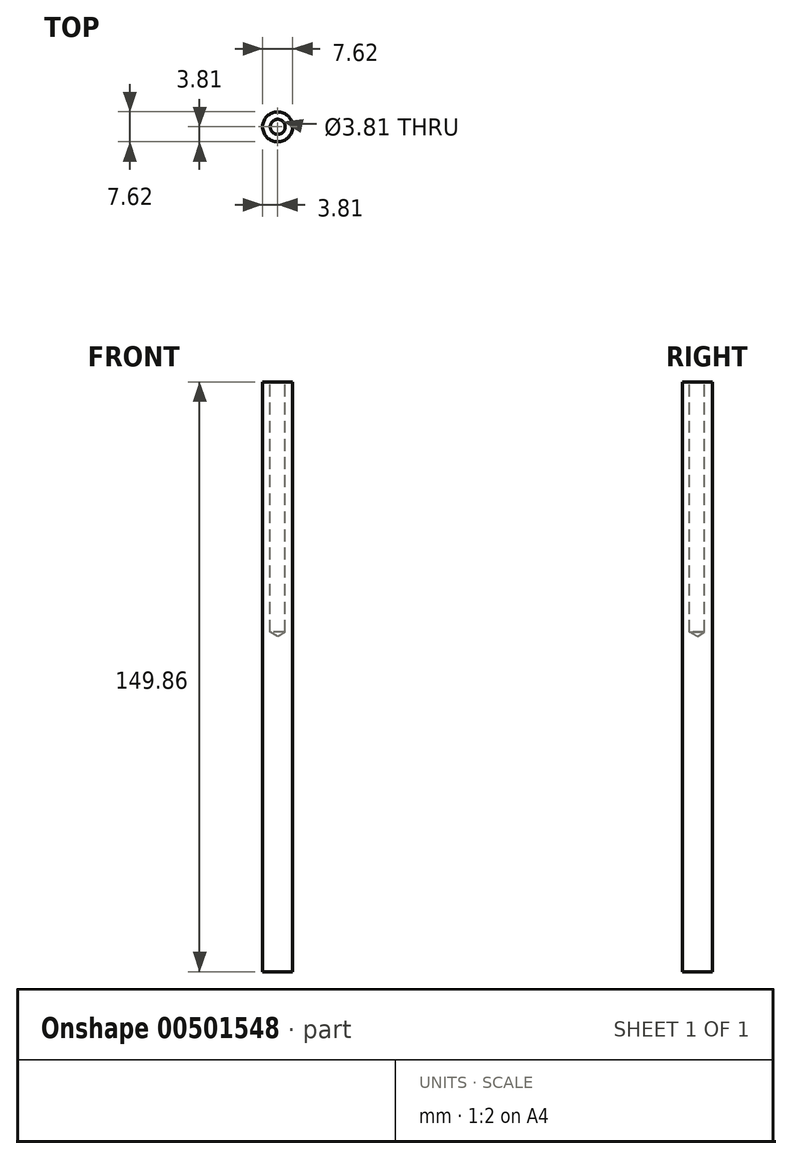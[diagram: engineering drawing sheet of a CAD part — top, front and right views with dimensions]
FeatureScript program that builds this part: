
annotation { "Feature Type Name" : "Feature", "Feature Type Description" : "" }
export const myFeature = defineFeature(function(context is Context, id is Id, definition is map)
    precondition{}
    {
        {
            var Q0;
            Q0=qCreatedBy(makeId("Top.planeOp"),FACE);
            var sketch = newSketch(context, id + "F0", { "sketchPlane" : qUnion([Q0])});
            skCircle(sketch, "E0", {"center": v(0, 0) * mm, "radius": 3.81 * mm});
            skSolve(sketch);
        }
        {
            var Q0;
            Q0=makeQuery(id+"F0.imprint","IMPRINT",FACE,{"disambiguationData":[TD([[makeQuery(id+"F0.imprint","IMPRINT",EDGE,{"derivedFrom":sQuery(id+"F0.wireOp",EDGE,"E0")}),1.0]])]});
            extrude(context, id + "F1", {"entities" : qUnion([Q0]), "depth" : 149.86 * mm});
        }
        {
            var Q0;
            Q0=makeQuery(id+"F1.opExtrude","CAP_FACE",FACE,{"disambiguationData":[OSD([sQuery(id+"F0.wireOp",EDGE,"E0")])],"isStart":false});
            var sketch = newSketch(context, id + "F2", { "sketchPlane" : qUnion([Q0])});
            skPoint(sketch, "E1", {"position": v(0, 0) * mm});
            skSolve(sketch);
        }
        {
            var Q0;
            Q0=sQuery(id+"F2.wireOp",VERTEX,"E1");
            var Q1;
            Q1=makeQuery(id+"F1.opExtrude","SWEPT_BODY",BODY,{"disambiguationData":[OSD([sQuery(id+"F0.wireOp",EDGE,"E0")])]});
            hole(context, id + "F3", {"style" : HoleStyle.SIMPLE, "endStyle" : HoleEndStyle.BLIND, "holeDiameter" : 3.8 * mm, "holeDepth" : 63.5 * mm, "isTappedThrough" : true, "tappedDepth" : 12.7 * mm, "tapClearance" : 3, "locations" : qUnion([Q0]), "scope" : qUnion([Q1])});
        }
    });
